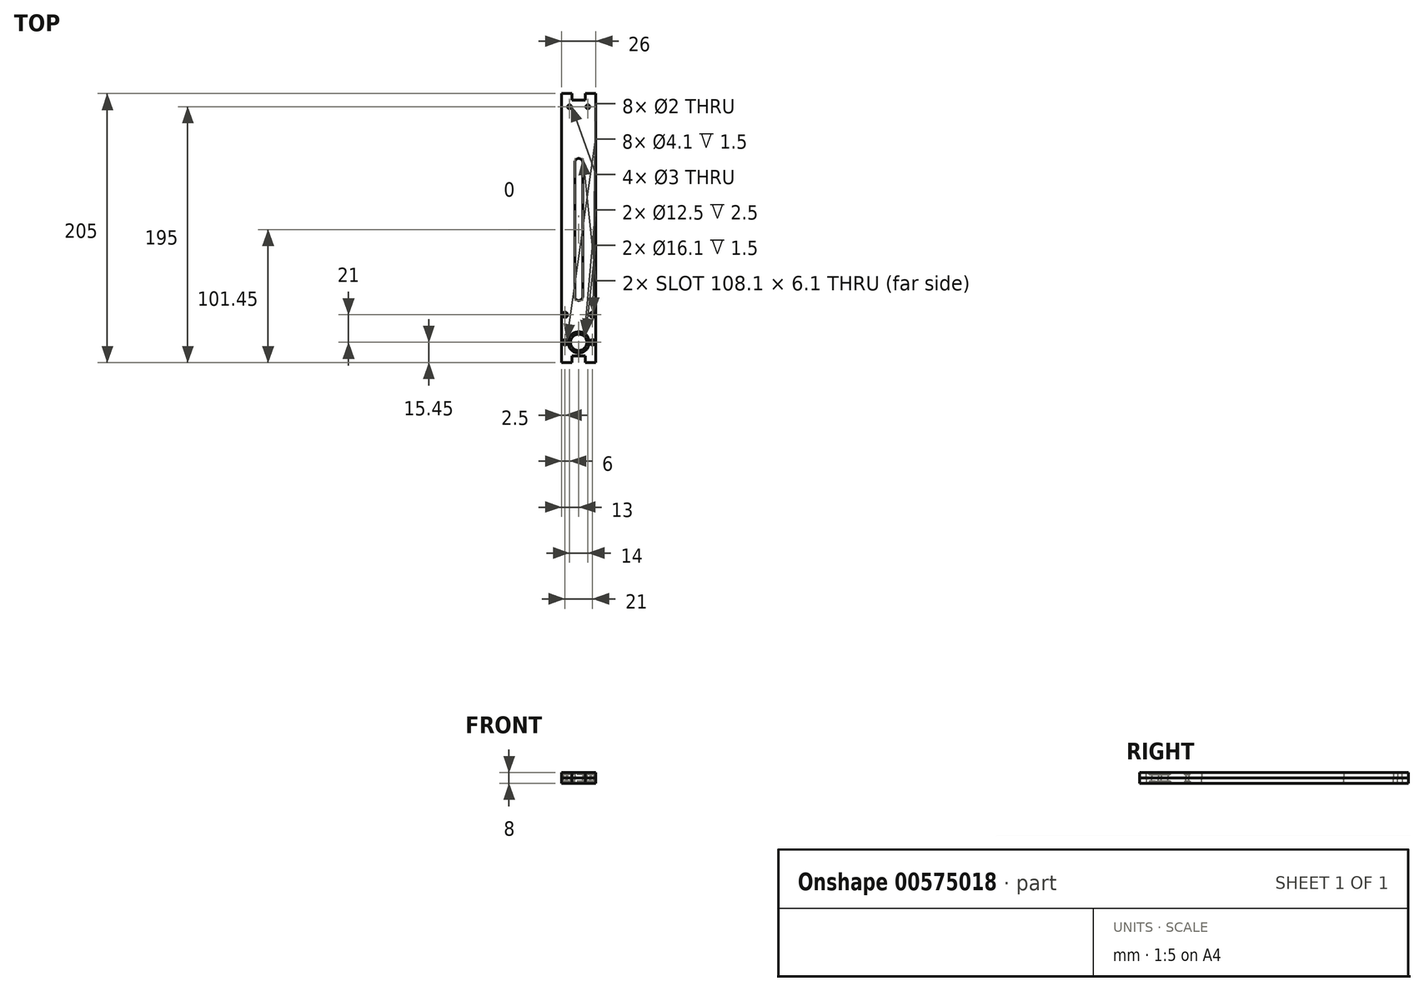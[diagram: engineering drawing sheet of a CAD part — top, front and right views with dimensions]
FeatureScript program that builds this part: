
annotation { "Feature Type Name" : "Feature", "Feature Type Description" : "" }
export const myFeature = defineFeature(function(context is Context, id is Id, definition is map)
    precondition{}
    {
        {
            var Q0;
            Q0=qCreatedBy(makeId("Top.planeOp"),FACE);
            var sketch = newSketch(context, id + "F0", { "sketchPlane" : qUnion([Q0])});
            skArc(sketch, "E0", {"start": v(3.05, 51) * mm, "mid": v(0, 54.05) * mm, "end": v(-3.05, 51) * mm});
            skArc(sketch, "E1.MirrorC", {"start": v(3.05, -51) * mm, "mid": v(0, -54.05) * mm, "end": v(-3.05, -51) * mm});
            skLineSegment(sketch, "E2", {"start": v(-3.05, 51) * mm, "end": v(-3.05, -51) * mm});
            skLineSegment(sketch, "E3.MirrorCS", {"start": v(3.05, 51) * mm, "end": v(3.05, -51) * mm});
            skCircle(sketch, "E4", {"center": v(-10.5, -65) * mm, "radius": 1 * mm});
            skCircle(sketch, "E5.MirrorC", {"center": v(10.5, -65) * mm, "radius": 1 * mm});
            skCircle(sketch, "E6", {"center": v(-10.5, -86) * mm, "radius": 1 * mm});
            skCircle(sketch, "E7.MirrorC", {"center": v(10.5, -86) * mm, "radius": 1 * mm});
            skArc(sketch, "E8", {"start": v(6.25, -86) * mm, "mid": v(0, -79.75) * mm, "end": v(-6.25, -86) * mm});
            skLineSegment(sketch, "E9", {"start": v(-6.25, -101.45) * mm, "end": v(-13, -101.45) * mm});
            skLineSegment(sketch, "E10", {"start": v(-13, -101.45) * mm, "end": v(-13, 98.55) * mm});
            skPoint(sketch, "E11", {"position": v(0, -92.25) * mm});
            skLineSegment(sketch, "E12", {"start": v(-13, 98.55) * mm, "end": v(0, 98.55) * mm});
            skLineSegment(sketch, "E13.MirrorCS", {"start": v(13, 98.55) * mm, "end": v(0, 98.55) * mm});
            skLineSegment(sketch, "E14.MirrorCS", {"start": v(13, -101.45) * mm, "end": v(13, 98.55) * mm});
            skLineSegment(sketch, "E15.MirrorCS", {"start": v(6.25, -101.45) * mm, "end": v(13, -101.45) * mm});
            skLineSegment(sketch, "E16", {"start": v(-6.25, -86) * mm, "end": v(-6.25, -101.45) * mm});
            skLineSegment(sketch, "E17.MirrorCS", {"start": v(6.25, -86) * mm, "end": v(6.25, -101.45) * mm});
            skPoint(sketch, "E18.orphan", {"position": v(0, -101.45) * mm});
            skPoint(sketch, "E19", {"position": v(0, -54.05) * mm});
            skPoint(sketch, "E20", {"position": v(0, 54.05) * mm});
            skCircle(sketch, "E21", {"center": v(-7, 93.55) * mm, "radius": 1.5 * mm});
            skCircle(sketch, "E22.MirrorC", {"center": v(7, 93.55) * mm, "radius": 1.5 * mm});
            skArc(sketch, "E23", {"start": v(-6.25, -86) * mm, "mid": v(0, -92.25) * mm, "end": v(6.25, -86) * mm});
            skLineSegment(sketch, "E24", {"start": v(-6.25, -101.45) * mm, "end": v(6.25, -101.45) * mm});
            skSolve(sketch);
        }
        {
            var Q0;
            Q0 = qSketchRegion(id + "F0", true);
            extrude(context, id + "F1", {"entities" : qUnion([Q0]), "depth" : 4 * mm, "offsetDistance" : 25 * mm});
        }
        {
            var Q0;
            Q0=makeQuery(id+"F1.opExtrude","CAP_FACE",FACE,{"disambiguationData":[OSD([sQuery(id+"F0.wireOp",EDGE,"E0"),sQuery(id+"F0.wireOp",EDGE,"E1.MirrorC"),sQuery(id+"F0.wireOp",EDGE,"E2"),sQuery(id+"F0.wireOp",EDGE,"E3.MirrorCS"),sQuery(id+"F0.wireOp",EDGE,"E4"),sQuery(id+"F0.wireOp",EDGE,"E5.MirrorC"),sQuery(id+"F0.wireOp",EDGE,"E6"),sQuery(id+"F0.wireOp",EDGE,"E7.MirrorC"),sQuery(id+"F0.wireOp",EDGE,"E8"),sQuery(id+"F0.wireOp",EDGE,"E9"),sQuery(id+"F0.wireOp",EDGE,"E10"),sQuery(id+"F0.wireOp",EDGE,"E12"),sQuery(id+"F0.wireOp",EDGE,"E13.MirrorCS"),sQuery(id+"F0.wireOp",EDGE,"E14.MirrorCS"),sQuery(id+"F0.wireOp",EDGE,"E15.MirrorCS"),sQuery(id+"F0.wireOp",EDGE,"E16"),sQuery(id+"F0.wireOp",EDGE,"E17.MirrorCS")])],"isStart":false});
            var sketch = newSketch(context, id + "F2", { "sketchPlane" : qUnion([Q0])});
            skCircle(sketch, "E25", {"center": v(0, -86) * mm, "radius": 8.05 * mm});
            skCircle(sketch, "E26", {"center": v(-10.5, -86) * mm, "radius": 2.05 * mm});
            skCircle(sketch, "E27", {"center": v(-10.5, -65) * mm, "radius": 2.05 * mm});
            skCircle(sketch, "E28.MirrorC", {"center": v(10.5, -65) * mm, "radius": 2.05 * mm});
            skCircle(sketch, "E29.MirrorC", {"center": v(10.5, -86) * mm, "radius": 2.05 * mm});
            skSolve(sketch);
        }
        {
            var Q0;
            Q0 = qSketchRegion(id + "F2", true);
            extrude(context, id + "F3", {"entities" : qUnion([Q0]), "operationType" : NewBodyOperationType.REMOVE, "oppositeDirection" : true, "depth" : 1.5 * mm, "offsetDistance" : 25 * mm});
        }
        {
            var Q0;
            Q0=makeQuery(id+"F1.opExtrude","CAP_FACE",FACE,{"disambiguationData":[OSD([sQuery(id+"F0.wireOp",EDGE,"E0"),sQuery(id+"F0.wireOp",EDGE,"E1.MirrorC"),sQuery(id+"F0.wireOp",EDGE,"E2"),sQuery(id+"F0.wireOp",EDGE,"E3.MirrorCS"),sQuery(id+"F0.wireOp",EDGE,"E4"),sQuery(id+"F0.wireOp",EDGE,"E5.MirrorC"),sQuery(id+"F0.wireOp",EDGE,"E6"),sQuery(id+"F0.wireOp",EDGE,"E7.MirrorC"),sQuery(id+"F0.wireOp",EDGE,"E8"),sQuery(id+"F0.wireOp",EDGE,"E9"),sQuery(id+"F0.wireOp",EDGE,"E10"),sQuery(id+"F0.wireOp",EDGE,"E12"),sQuery(id+"F0.wireOp",EDGE,"E13.MirrorCS"),sQuery(id+"F0.wireOp",EDGE,"E14.MirrorCS"),sQuery(id+"F0.wireOp",EDGE,"E15.MirrorCS"),sQuery(id+"F0.wireOp",EDGE,"E21"),sQuery(id+"F0.wireOp",EDGE,"E22.MirrorC"),sQuery(id+"F0.wireOp",EDGE,"E23"),sQuery(id+"F0.wireOp",EDGE,"E24")])],"isStart":false});
            var sketch = newSketch(context, id + "F4", { "sketchPlane" : qUnion([Q0])});
            skLineSegment(sketch, "E30", {"start": v(-13, -96.45) * mm, "end": v(13, -96.45) * mm});
            skLineSegment(sketch, "E31", {"start": v(-5, -96.45) * mm, "end": v(-5, -101.45) * mm});
            skLineSegment(sketch, "E32.MirrorCS", {"start": v(5, -96.45) * mm, "end": v(5, -101.45) * mm});
            skSolve(sketch);
        }
        {
            var Q0;
            {var subQ0=sQuery(id+"F4.wireOp",EDGE,"E31");Q0=makeQuery(id+"F4.imprint","IMPRINT",FACE,{"disambiguationData":[TD([[makeQuery(id+"F4.imprint","IMPRINT",EDGE,{"derivedFrom":subQ0}),1.0]])]});}
            extrude(context, id + "F5", {"entities" : qUnion([Q0]), "operationType" : NewBodyOperationType.REMOVE, "endBound" : BoundingType.THROUGH_ALL, "oppositeDirection" : true, "depth" : 25 * mm, "offsetDistance" : 25 * mm});
        }
        {
            var Q0;
            Q0=makeQuery(id+"F1.opExtrude","CAP_FACE",FACE,{"disambiguationData":[OSD([sQuery(id+"F0.wireOp",EDGE,"E0"),sQuery(id+"F0.wireOp",EDGE,"E1.MirrorC"),sQuery(id+"F0.wireOp",EDGE,"E2"),sQuery(id+"F0.wireOp",EDGE,"E3.MirrorCS"),sQuery(id+"F0.wireOp",EDGE,"E4"),sQuery(id+"F0.wireOp",EDGE,"E5.MirrorC"),sQuery(id+"F0.wireOp",EDGE,"E6"),sQuery(id+"F0.wireOp",EDGE,"E7.MirrorC"),sQuery(id+"F0.wireOp",EDGE,"E8"),sQuery(id+"F0.wireOp",EDGE,"E9"),sQuery(id+"F0.wireOp",EDGE,"E10"),sQuery(id+"F0.wireOp",EDGE,"E12"),sQuery(id+"F0.wireOp",EDGE,"E13.MirrorCS"),sQuery(id+"F0.wireOp",EDGE,"E14.MirrorCS"),sQuery(id+"F0.wireOp",EDGE,"E15.MirrorCS"),sQuery(id+"F0.wireOp",EDGE,"E21"),sQuery(id+"F0.wireOp",EDGE,"E22.MirrorC"),sQuery(id+"F0.wireOp",EDGE,"E23"),sQuery(id+"F0.wireOp",EDGE,"E24")])],"isStart":false});
            var sketch = newSketch(context, id + "F6", { "sketchPlane" : qUnion([Q0])});
            skLineSegment(sketch, "E33", {"start": v(-13, 98.55) * mm, "end": v(-13, 103.55) * mm});
            skLineSegment(sketch, "E34", {"start": v(-13, 103.55) * mm, "end": v(-5, 103.55) * mm});
            skLineSegment(sketch, "E35", {"start": v(-5, 103.55) * mm, "end": v(-5, 98.55) * mm});
            skLineSegment(sketch, "E36", {"start": v(-5, 98.55) * mm, "end": v(-13, 98.55) * mm});
            skLineSegment(sketch, "E37.MirrorCS", {"start": v(13, 103.55) * mm, "end": v(5, 103.55) * mm});
            skLineSegment(sketch, "E38.MirrorCS", {"start": v(13, 98.55) * mm, "end": v(13, 103.55) * mm});
            skLineSegment(sketch, "E39.MirrorCS", {"start": v(5, 103.55) * mm, "end": v(5, 98.55) * mm});
            skLineSegment(sketch, "E40.MirrorCS", {"start": v(5, 98.55) * mm, "end": v(13, 98.55) * mm});
            skSolve(sketch);
        }
        {
            var Q0;
            Q0 = qSketchRegion(id + "F6", true);
            extrude(context, id + "F7", {"entities" : qUnion([Q0]), "operationType" : NewBodyOperationType.ADD, "oppositeDirection" : true, "depth" : 4 * mm, "offsetDistance" : 25 * mm});
        }
        {
            var Q0;
            Q0=makeQuery(id+"F1.opExtrude","SWEPT_BODY",BODY,{"disambiguationData":[OSD([sQuery(id+"F0.wireOp",EDGE,"E0"),sQuery(id+"F0.wireOp",EDGE,"E1.MirrorC"),sQuery(id+"F0.wireOp",EDGE,"E2"),sQuery(id+"F0.wireOp",EDGE,"E3.MirrorCS"),sQuery(id+"F0.wireOp",EDGE,"E4"),sQuery(id+"F0.wireOp",EDGE,"E5.MirrorC"),sQuery(id+"F0.wireOp",EDGE,"E6"),sQuery(id+"F0.wireOp",EDGE,"E7.MirrorC"),sQuery(id+"F0.wireOp",EDGE,"E8"),sQuery(id+"F0.wireOp",EDGE,"E9"),sQuery(id+"F0.wireOp",EDGE,"E10"),sQuery(id+"F0.wireOp",EDGE,"E12"),sQuery(id+"F0.wireOp",EDGE,"E13.MirrorCS"),sQuery(id+"F0.wireOp",EDGE,"E14.MirrorCS"),sQuery(id+"F0.wireOp",EDGE,"E15.MirrorCS"),sQuery(id+"F0.wireOp",EDGE,"E21"),sQuery(id+"F0.wireOp",EDGE,"E22.MirrorC"),sQuery(id+"F0.wireOp",EDGE,"E23"),sQuery(id+"F0.wireOp",EDGE,"E24")])]});
            var Q1;
            Q1=qCreatedBy(makeId("Top.planeOp"),FACE);
            mirror(context, id + "F8", {"entities" : qUnion([Q0]), "mirrorPlane" : qUnion([Q1])});
        }
    });
